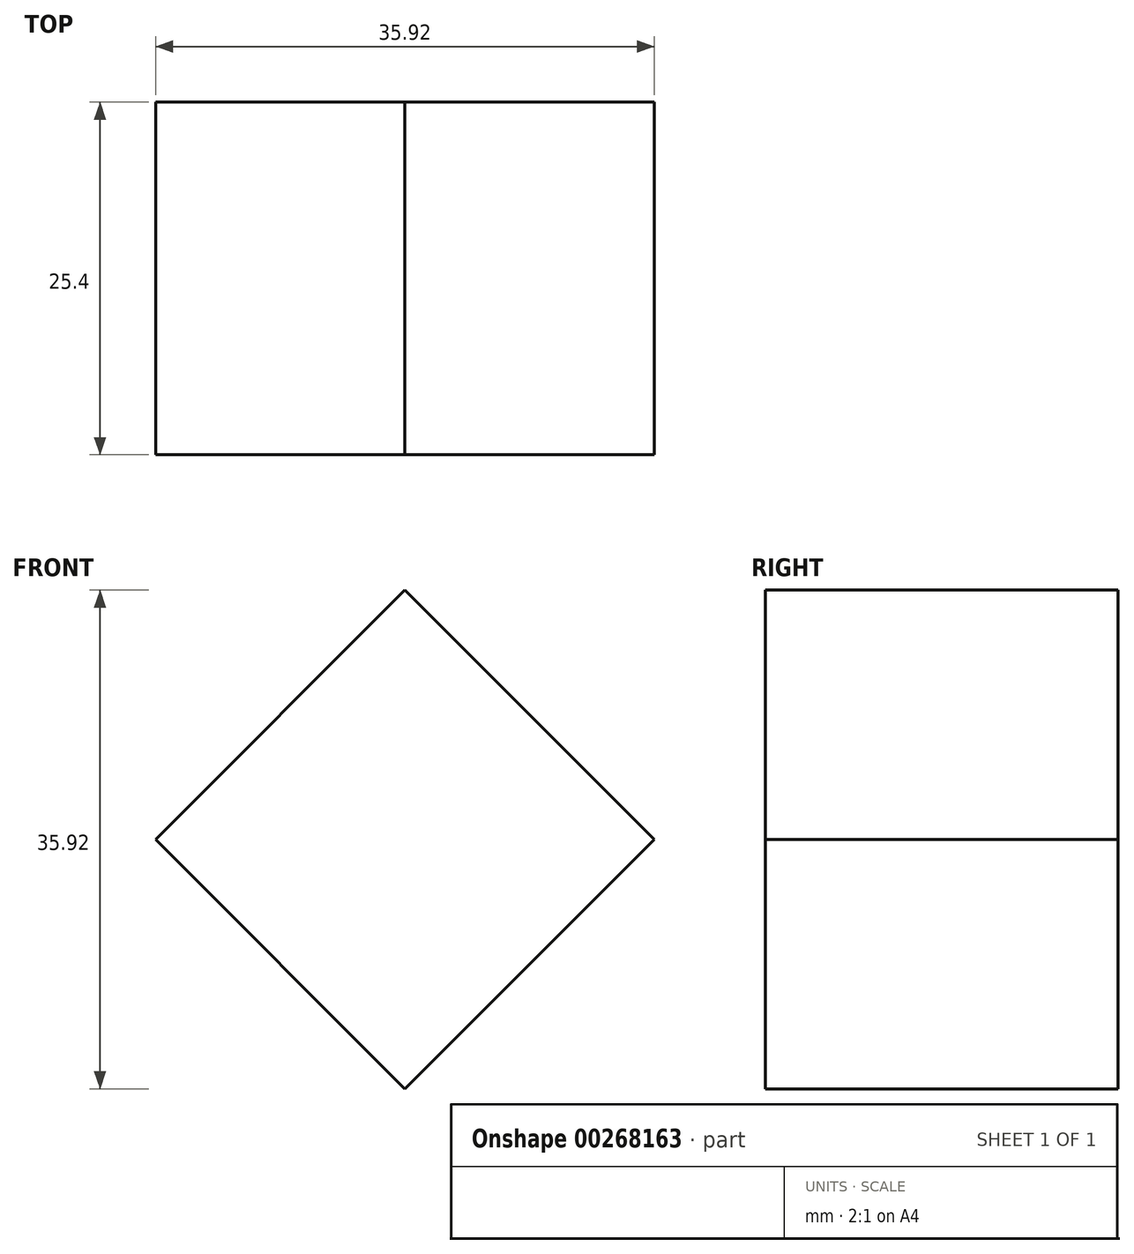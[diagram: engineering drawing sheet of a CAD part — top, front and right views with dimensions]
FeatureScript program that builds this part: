
annotation { "Feature Type Name" : "Feature", "Feature Type Description" : "" }
export const myFeature = defineFeature(function(context is Context, id is Id, definition is map)
    precondition{}
    {
        {
            var Q0;
            Q0=qCreatedBy(makeId("Front.planeOp"),FACE);
            var sketch = newSketch(context, id + "F0", { "sketchPlane" : qUnion([Q0])});
            skLineSegment(sketch, "E0", {"start": v(0, 17.96) * mm, "end": v(-17.96, 0) * mm});
            skLineSegment(sketch, "E1", {"start": v(-17.96, 0) * mm, "end": v(0, -17.96) * mm});
            skLineSegment(sketch, "E2", {"start": v(0, -17.96) * mm, "end": v(17.96, 0) * mm});
            skLineSegment(sketch, "E3", {"start": v(17.96, 0) * mm, "end": v(0, 17.96) * mm});
            skSolve(sketch);
        }
        {
            var Q0;
            Q0 = qSketchRegion(id + "F0", true);
            extrude(context, id + "F1", {"entities" : qUnion([Q0]), "depth" : 25.4 * mm});
        }
    });
